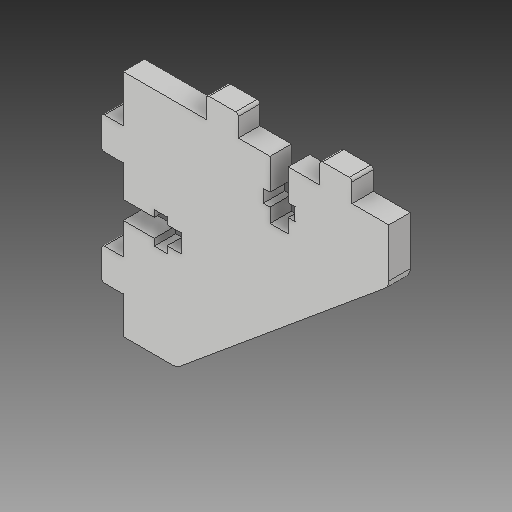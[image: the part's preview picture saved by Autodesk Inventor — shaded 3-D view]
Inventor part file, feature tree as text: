
AUTODESK INVENTOR PART (.ipt)
format: ipt  version: 2019 (Build 230136000, 136)  size: 268,288 bytes
history: native  units: in
note: dims shown in document units (in); Inventor stores cm internally (conversion verified against a paired STEP export)
features: reference x6, extrude x5, sketch x5, other x5, fillet x2, projected_geometry x1, helix x1
ambient origin geometry x8: Origin, YZ Plane, XZ Plane, XY Plane, X Axis, Y Axis, Z Axis, Center Point
bodies: Solid1 (feature_tree)
feature tree (25):
  extrude  "Extrusion1"  Depth=0.3937in
  fillet  "Fillet1"  Radius=0.1575in
  extrude  "Extrusion2"  Depth=0.1575in TaperAngle=0.0deg
  extrude  "Extrusion3"  Depth=0.1575in
  extrude  "Extrusion4"  Depth=1.0in TaperAngle=0.0deg
  extrude  "Extrusion5"  Depth=0.0197in
  fillet  "Fillet2"  [1 undecoded]
  sketch  "Sketch1"  dims[d0=0.3937in d1=0.3937in d2=0.1575in d3=0.0in]
  reference  "Reference1"
  sketch  "Sketch2"  dims[d4=0.0787in d5=0.1575in d6=0.0in]
  reference  "Reference3"
  reference  "Reference4"
  sketch  "Sketch3"  dims[d7=0.1575in d8=0.0in d9=0.0079in]
  reference  "Reference5"
  reference  "Reference6"
  reference  "Reference7"
  sketch  "Sketch4"  dims[d10=0.0079in d11=1.0in d12=0.0in]
  projected_geometry  "Projected Loop1"
  sketch  "Sketch5"  dims[d13=1.0in d14=0.0in d15=0.0197in]
  other  "<userpath>\Documents\CAD Files\Helix DLP\Helix DLP.iam"
  helix  "Helix DLP.iam"  [1 undecoded]
  other  "Motor Brace_1:1"
  other  "Maker_jigsaw_template:2"
  other  "Maker_jigsaw_template:3"
  other  "Motor_brace_2:1"
note: 2 required parameter values undecoded (feature->parameter linkage not recoverable at this tier; creation-order binding heuristic only, values carry confidence <= 0.55)
